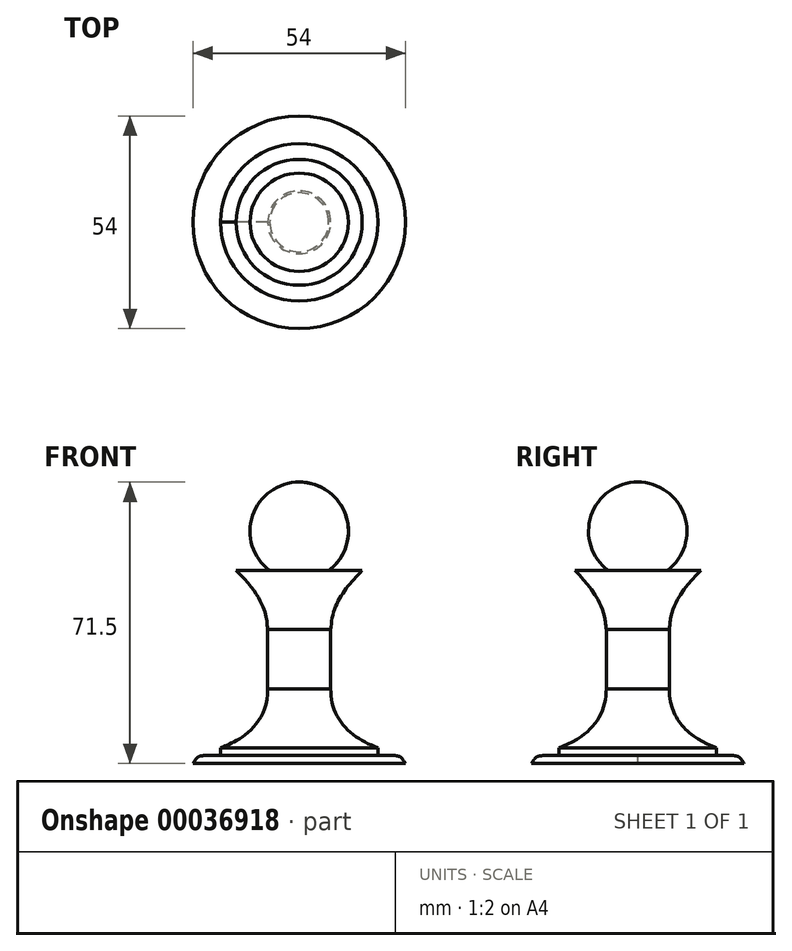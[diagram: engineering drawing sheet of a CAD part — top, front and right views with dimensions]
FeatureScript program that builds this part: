
annotation { "Feature Type Name" : "Feature", "Feature Type Description" : "" }
export const myFeature = defineFeature(function(context is Context, id is Id, definition is map)
    precondition{}
    {
        {
            var Q0;
            Q0=qCreatedBy(makeId("Front.planeOp"),FACE);
            var sketch = newSketch(context, id + "F0", { "sketchPlane" : qUnion([Q0])});
            skLineSegment(sketch, "E0", {"start": v(-22.24, -10.58) * mm, "end": v(-13.74, -10.58) * mm});
            skLineSegment(sketch, "E1", {"start": v(-21.74, -25.58) * mm, "end": v(-21.74, -40.58) * mm});
            skLineSegment(sketch, "E2", {"start": v(-9.74, -57.58) * mm, "end": v(-5.74, -57.58) * mm});
            skLineSegment(sketch, "E3", {"start": v(-29.74, -59.58) * mm, "end": v(-2.74, -59.58) * mm});
            skArc(sketch, "E4", {"start": v(-22.24, -10.58) * mm, "mid": v(-17.88, 3.37) * mm, "end": v(-29.74, 11.92) * mm});
            skFitSpline(sketch, "E5", {"points": [v(-2.74, -59.58) * mm, v(-5.74, -57.58) * mm], "startDerivative": vector(-2.4, 3.16) * mm, "endDerivative": vector(-6.6, -0.05) * mm});
            skFitSpline(sketch, "E6", {"points": [v(-13.74, -10.58) * mm, v(-21.74, -25.58) * mm], "startDerivative": vector(-26.47, -25.46) * mm, "endDerivative": vector(-1.18, -3.76) * mm});
            skFitSpline(sketch, "E7", {"points": [v(-21.74, -40.58) * mm, v(-9.74, -55.58) * mm], "startDerivative": vector(-0.08, -33.44) * mm, "endDerivative": vector(5.11, -2.24) * mm});
            skLineSegment(sketch, "E8", {"start": v(-9.74, -55.58) * mm, "end": v(-9.74, -57.58) * mm});
            skLineSegment(sketch, "E9", {"start": v(-29.74, -59.58) * mm, "end": v(-29.74, 11.92) * mm});
            skSolve(sketch);
        }
        {
            var Q0;
            Q0 = qSketchRegion(id + "F0", true);
            var Q1;
            Q1=sQuery(id+"F0.wireOp",EDGE,"E9");
            revolve(context, id + "F1", {"entities" : qUnion([Q0]), "axis" : qUnion([Q1]), "revolveType" : RevolveType.FULL});
        }
    });
